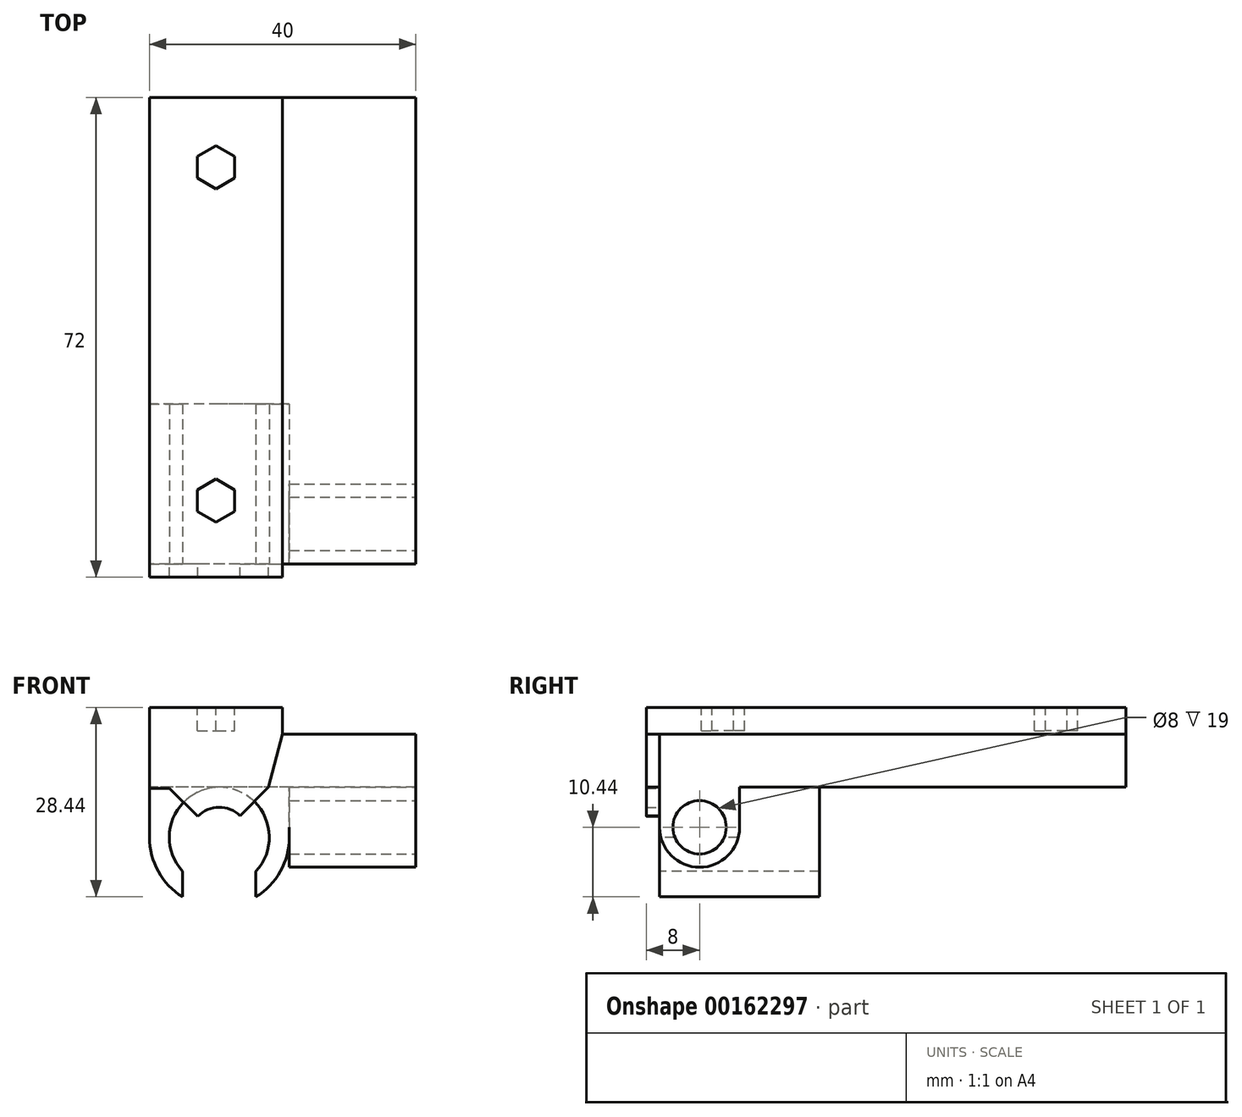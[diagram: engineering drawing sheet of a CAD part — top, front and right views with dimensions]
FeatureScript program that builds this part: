
annotation { "Feature Type Name" : "Feature", "Feature Type Description" : "" }
export const myFeature = defineFeature(function(context is Context, id is Id, definition is map)
    precondition{}
    {
        {
            var Q0;
            Q0=qCreatedBy(makeId("Front.planeOp"),FACE);
            var sketch = newSketch(context, id + "F0", { "sketchPlane" : qUnion([Q0])});
            skLineSegment(sketch, "E0.bottom", {"start": v(20, -12) * mm, "end": v(-20, -12) * mm});
            skLineSegment(sketch, "E0.top", {"start": v(20, -4) * mm, "end": v(0, -4) * mm});
            skLineSegment(sketch, "E0.left", {"start": v(20, -12) * mm, "end": v(20, -4) * mm});
            skLineSegment(sketch, "E0.right", {"start": v(-20, -12) * mm, "end": v(-20, -4) * mm});
            skPoint(sketch, "E0.middle", {"position": v(0, -8) * mm});
            skLineSegment(sketch, "E1.top", {"start": v(-20, 0) * mm, "end": v(0, 0) * mm});
            skLineSegment(sketch, "E1.left", {"start": v(-20, -4) * mm, "end": v(-20, 0) * mm});
            skLineSegment(sketch, "E1.right", {"start": v(0, -4) * mm, "end": v(0, 0) * mm});
            skSolve(sketch);
        }
        {
            var Q0;
            Q0 = qSketchRegion(id + "F0", true);
            extrude(context, id + "F1", {"entities" : qUnion([Q0]), "depth" : 70 * mm});
        }
        {
            var Q0;
            Q0=makeQuery(id+"F1.opExtrude","CAP_FACE",FACE,{"disambiguationData":[OSD([sQuery(id+"F0.wireOp",EDGE,"E0.bottom"),sQuery(id+"F0.wireOp",EDGE,"E0.top"),sQuery(id+"F0.wireOp",EDGE,"E0.left"),sQuery(id+"F0.wireOp",EDGE,"E0.right"),sQuery(id+"F0.wireOp",EDGE,"E1.top"),sQuery(id+"F0.wireOp",EDGE,"E1.left"),sQuery(id+"F0.wireOp",EDGE,"E1.right")])],"isStart":false});
            var sketch = newSketch(context, id + "F2", { "sketchPlane" : qUnion([Q0])});
            skArc(sketch, "E2", {"start": v(-4, -24.6) * mm, "mid": v(-9.5, -12) * mm, "end": v(-15, -24.6) * mm});
            skArc(sketch, "E3", {"start": v(-20, -19.5) * mm, "mid": v(-18.67, -24.62) * mm, "end": v(-15, -28.44) * mm});
            skLineSegment(sketch, "E4", {"start": v(-20, -12) * mm, "end": v(-20, -24.6) * mm, "construction": true});
            skLineSegment(sketch, "E5", {"start": v(-20, -12) * mm, "end": v(-20, -19.5) * mm});
            skLineSegment(sketch, "E6", {"start": v(1, -19.5) * mm, "end": v(1, -12) * mm});
            skLineSegment(sketch, "E7", {"start": v(-20, -12) * mm, "end": v(1, -12) * mm});
            skLineSegment(sketch, "E8", {"start": v(-15, -24.6) * mm, "end": v(-15, -28.44) * mm});
            skLineSegment(sketch, "E9", {"start": v(-4, -24.6) * mm, "end": v(-4, -28.44) * mm});
            skArc(sketch, "E10.trimOffspring", {"start": v(-4, -28.44) * mm, "mid": v(-0.33, -24.62) * mm, "end": v(1, -19.5) * mm});
            skSolve(sketch);
        }
        {
            var Q0;
            Q0 = qSketchRegion(id + "F2", true);
            extrude(context, id + "F3", {"entities" : qUnion([Q0]), "operationType" : NewBodyOperationType.ADD, "oppositeDirection" : true, "depth" : 24 * mm});
        }
        {
            var Q0;
            Q0=qCreatedBy(makeId("Front.planeOp"),FACE);
            cPlane(context, id + "F4", {"entities" : qUnion([Q0]), "cplaneType" : CPlaneType.OFFSET, "offset" : 35 * mm, "width" : 150 * mm, "height" : 150 * mm});
        }
        {
            var Q0;
            {var subQ0=sQuery(id+"F2.wireOp",EDGE,"E7");var subQ1=sQuery(id+"F2.wireOp",EDGE,"E2");Q0=makeQuery(id+"F3.boolean.opBoolean","MERGE",FACE,{"derivedFrom":[makeQuery(id+"F1.opExtrude","CAP_FACE",FACE,{"disambiguationData":[OSD([sQuery(id+"F0.wireOp",EDGE,"E0.bottom"),sQuery(id+"F0.wireOp",EDGE,"E0.top"),sQuery(id+"F0.wireOp",EDGE,"E0.left"),sQuery(id+"F0.wireOp",EDGE,"E0.right"),sQuery(id+"F0.wireOp",EDGE,"E1.top"),sQuery(id+"F0.wireOp",EDGE,"E1.left"),sQuery(id+"F0.wireOp",EDGE,"E1.right")])],"isStart":false}),makeQuery(id+"F3.opExtrude","CAP_FACE",FACE,{"disambiguationData":[OSD([subQ1,sQuery(id+"F2.wireOp",EDGE,"E6"),subQ0,sQuery(id+"F2.wireOp",EDGE,"E9"),sQuery(id+"F2.wireOp",EDGE,"E10.trimOffspring")])],"isStart":true}),makeQuery(id+"F3.opExtrude","CAP_FACE",FACE,{"disambiguationData":[OSD([subQ1,sQuery(id+"F2.wireOp",EDGE,"E3"),sQuery(id+"F2.wireOp",EDGE,"E5"),subQ0,sQuery(id+"F2.wireOp",EDGE,"E8")])],"isStart":true})]});}
            var sketch = newSketch(context, id + "F5", { "sketchPlane" : qUnion([Q0])});
            skLineSegment(sketch, "E11", {"start": v(-12.71, -16.35) * mm, "end": v(-17, -12.15) * mm});
            skLineSegment(sketch, "E12", {"start": v(-6.35, -16.29) * mm, "end": v(-2.15, -12) * mm});
            skArc(sketch, "E13", {"start": v(-6.35, -16.29) * mm, "mid": v(-9.55, -15) * mm, "end": v(-12.71, -16.35) * mm});
            skLineSegment(sketch, "E14", {"start": v(-17, -12.15) * mm, "end": v(-20, -12.15) * mm});
            skLineSegment(sketch, "E15", {"start": v(-20, -12.15) * mm, "end": v(-20, 0) * mm});
            skLineSegment(sketch, "E16", {"start": v(-20, 0) * mm, "end": v(0, 0) * mm});
            skLineSegment(sketch, "E17", {"start": v(-2.15, -12) * mm, "end": v(0, -4) * mm});
            skLineSegment(sketch, "E18", {"start": v(0, -4) * mm, "end": v(0, 0) * mm});
            skSolve(sketch);
        }
        {
            var Q0;
            Q0 = qSketchRegion(id + "F5", true);
            extrude(context, id + "F6", {"entities" : qUnion([Q0]), "operationType" : NewBodyOperationType.ADD, "depth" : 2 * mm});
        }
        {
            var Q0;
            {var subQ0=sQuery(id+"F2.wireOp",EDGE,"E9");var subQ1=sQuery(id+"F2.wireOp",EDGE,"E6");var subQ5=sQuery(id+"F2.wireOp",EDGE,"E2");var subQ6=sQuery(id+"F2.wireOp",EDGE,"E7");var subQ8=sQuery(id+"F0.wireOp",EDGE,"E0.bottom");var subQ9=sQuery(id+"F0.wireOp",EDGE,"E0.top");var subQ10=sQuery(id+"F0.wireOp",EDGE,"E0.left");var subQ11=sQuery(id+"F2.wireOp",EDGE,"E10.trimOffspring");var subQ12=sQuery(id+"F2.wireOp",EDGE,"E8");var subQ13=sQuery(id+"F0.wireOp",EDGE,"E1.right");Q0=makeQuery(id+"F6.boolean.opBoolean","SPLIT",FACE,{"disambiguationData":[TD([makeQuery(id+"F1.opExtrude","SWEPT_FACE",FACE,{"disambiguationData":[OSD([subQ8])]})])],"derivedFrom":makeQuery(id+"F3.boolean.opBoolean","MERGE",FACE,{"derivedFrom":[makeQuery(id+"F1.opExtrude","CAP_FACE",FACE,{"disambiguationData":[OSD([subQ8,subQ9,subQ10,sQuery(id+"F0.wireOp",EDGE,"E0.right"),sQuery(id+"F0.wireOp",EDGE,"E1.top"),sQuery(id+"F0.wireOp",EDGE,"E1.left"),subQ13])],"isStart":false}),makeQuery(id+"F3.opExtrude","CAP_FACE",FACE,{"disambiguationData":[OSD([subQ5,subQ1,subQ6,subQ0,subQ11])],"isStart":true}),makeQuery(id+"F3.opExtrude","CAP_FACE",FACE,{"disambiguationData":[OSD([subQ5,sQuery(id+"F2.wireOp",EDGE,"E3"),sQuery(id+"F2.wireOp",EDGE,"E5"),subQ6,subQ12])],"isStart":true})]})});}
            cPlane(context, id + "F7", {"entities" : qUnion([Q0]), "cplaneType" : CPlaneType.OFFSET, "offset" : 12 * mm, "oppositeDirection" : true, "width" : 150 * mm, "height" : 150 * mm});
        }
        {
            var Q0;
            Q0=makeQuery(id+"F1.opExtrude","SWEPT_FACE",FACE,{"disambiguationData":[OSD([sQuery(id+"F0.wireOp",EDGE,"E0.left")])]});
            var sketch = newSketch(context, id + "F8", { "sketchPlane" : qUnion([Q0])});
            skArc(sketch, "E19", {"start": v(-70, -18) * mm, "mid": v(-64, -24) * mm, "end": v(-58, -18) * mm});
            skCircle(sketch, "E20", {"center": v(-64, -18) * mm, "radius": 4 * mm});
            skLineSegment(sketch, "E21", {"start": v(-70, -12) * mm, "end": v(-70, -18) * mm});
            skLineSegment(sketch, "E22", {"start": v(-58, -18) * mm, "end": v(-58, -12) * mm});
            skLineSegment(sketch, "E23", {"start": v(-70, -12) * mm, "end": v(-58, -12) * mm});
            skSolve(sketch);
        }
        {
            var Q0;
            Q0 = qSketchRegion(id + "F8", true);
            var Q1;
            Q1=makeQuery(id+"F3.opExtrude","SWEPT_FACE",FACE,{"disambiguationData":[OSD([sQuery(id+"F2.wireOp",EDGE,"E6")])]});
            extrude(context, id + "F9", {"entities" : qUnion([Q0]), "operationType" : NewBodyOperationType.ADD, "endBound" : BoundingType.UP_TO_SURFACE, "oppositeDirection" : true, "endBoundEntityFace" : qUnion([Q1]), "depth" : 25 * mm});
        }
        {
            var Q0;
            {var subQ0=sQuery(id+"F5.wireOp",EDGE,"E16");Q0=makeQuery(id+"Fi5MN1vpxqqN3R8_1.1.F6.boolean.opBoolean","MERGE",FACE,{"derivedFrom":[makeQuery(id+"F6.boolean.opBoolean","MERGE",FACE,{"derivedFrom":[makeQuery(id+"F1.opExtrude","SWEPT_FACE",FACE,{"disambiguationData":[OSD([sQuery(id+"F0.wireOp",EDGE,"E1.top")])]}),makeQuery(id+"F6.opExtrude","SWEPT_FACE",FACE,{"disambiguationData":[OSD([subQ0])]})]}),makeQuery(id+"Fi5MN1vpxqqN3R8_1.1.F6.opExtrude","SWEPT_FACE",FACE,{"disambiguationData":[OSD([subQ0])]})]});}
            var sketch = newSketch(context, id + "F10", { "sketchPlane" : qUnion([Q0])});
            skLineSegment(sketch, "E24", {"start": v(-20, -10.5) * mm, "end": v(0, -10.5) * mm, "construction": true});
            skLineSegment(sketch, "E25", {"start": v(-20, -60.5) * mm, "end": v(0, -60.5) * mm, "construction": true});
            skLineSegment(sketch, "E26", {"start": v(-10, 2) * mm, "end": v(-10, -72) * mm, "construction": true});
            skPoint(sketch, "E27", {"position": v(-10, -10.5) * mm});
            skPoint(sketch, "E28", {"position": v(-10, -60.5) * mm});
            skCircle(sketch, "E29.cCircle", {"center": v(-10, -10.5) * mm, "radius": 2.8 * mm, "construction": true});
            skLineSegment(sketch, "E29.0", {"start": v(-7.2, -8.88) * mm, "end": v(-7.2, -12.12) * mm});
            skLineSegment(sketch, "E29.1", {"start": v(-7.2, -12.12) * mm, "end": v(-10, -13.73) * mm});
            skLineSegment(sketch, "E29.2", {"start": v(-10, -13.73) * mm, "end": v(-12.8, -12.12) * mm});
            skLineSegment(sketch, "E29.3", {"start": v(-12.8, -12.12) * mm, "end": v(-12.8, -8.88) * mm});
            skLineSegment(sketch, "E29.4", {"start": v(-12.8, -8.88) * mm, "end": v(-10, -7.27) * mm});
            skLineSegment(sketch, "E29.5", {"start": v(-10, -7.27) * mm, "end": v(-7.2, -8.88) * mm});
            skPoint(sketch, "E29.0.midPoint", {"position": v(-7.2, -10.5) * mm});
            skCircle(sketch, "E30.cCircle", {"center": v(-10, -60.5) * mm, "radius": 2.8 * mm, "construction": true});
            skLineSegment(sketch, "E30.0", {"start": v(-7.2, -58.88) * mm, "end": v(-7.2, -62.12) * mm});
            skLineSegment(sketch, "E30.1", {"start": v(-7.2, -62.12) * mm, "end": v(-10, -63.73) * mm});
            skLineSegment(sketch, "E30.2", {"start": v(-10, -63.73) * mm, "end": v(-12.8, -62.12) * mm});
            skLineSegment(sketch, "E30.3", {"start": v(-12.8, -62.12) * mm, "end": v(-12.8, -58.88) * mm});
            skLineSegment(sketch, "E30.4", {"start": v(-12.8, -58.88) * mm, "end": v(-10, -57.27) * mm});
            skLineSegment(sketch, "E30.5", {"start": v(-10, -57.27) * mm, "end": v(-7.2, -58.88) * mm});
            skPoint(sketch, "E30.0.midPoint", {"position": v(-7.2, -60.5) * mm});
            skSolve(sketch);
        }
        {
            var Q0;
            Q0 = qSketchRegion(id + "F10", true);
            extrude(context, id + "F11", {"entities" : qUnion([Q0]), "operationType" : NewBodyOperationType.REMOVE, "oppositeDirection" : true, "depth" : 3.5 * mm});
        }
    });
